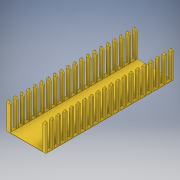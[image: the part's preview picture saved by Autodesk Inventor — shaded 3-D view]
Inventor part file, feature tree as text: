
AUTODESK INVENTOR PART (.ipt)
format: ipt  version: 2019 (Build 230136000, 136)  size: 592,896 bytes
history: native  units: in
note: dims shown in document units (in); Inventor stores cm internally (conversion verified against a paired STEP export)
features: other x14, extrude x3, sketch x3
ambient origin geometry x8: Origin, YZ Plane, XZ Plane, XY Plane, X Axis, Y Axis, Z Axis, Center Point
bodies: Solid1 (feature_tree)
feature tree (20):
  extrude  "Extrusion1"  Depth=2.0in TaperAngle=0.0deg
  extrude  "Extrusion2"  [1 undecoded]
  extrude  "Extrusion3"  [1 undecoded]
  other  "p2_XY"
  other  "p2_YZ"
  other  "p2_ZX"
  other  "p2_X"
  other  "p2_Y"
  other  "p2_Z"
  other  "p2_Center"
  other  "pin_XY"
  other  "pin_YZ"
  other  "pin_ZX"
  other  "pin_X"
  other  "pin_Y"
  other  "pin_Z"
  other  "pin_Center"
  sketch  "Sketch_1"  dims[d0=0.61in d1=0.0in d2=2.0in d3=0.0in]
  sketch  "Sketch_2"  dims[d4=100.0in d5=0.0in]
  sketch  "Sketch_5"
note: 2 required parameter values undecoded (feature->parameter linkage not recoverable at this tier; creation-order binding heuristic only, values carry confidence <= 0.55)
